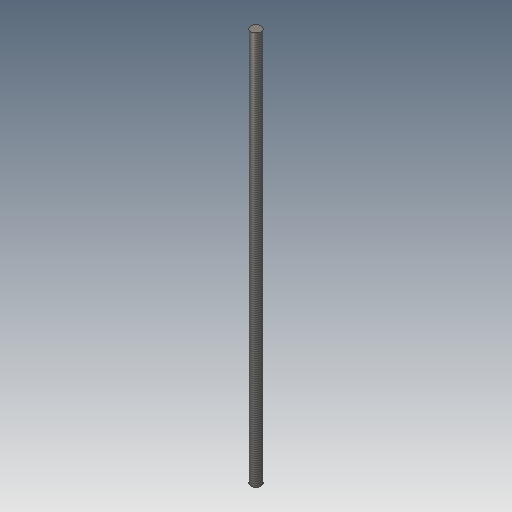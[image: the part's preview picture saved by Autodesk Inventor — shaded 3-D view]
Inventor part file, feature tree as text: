
AUTODESK INVENTOR PART (.ipt)
format: ipt  version: 2019 (Build 230136000, 136)  size: 87,552 bytes
history: native  units: mm
features: extrude x1, thread x1, sketch x1
ambient origin geometry x8: Origin, YZ Plane, XZ Plane, XY Plane, X Axis, Y Axis, Z Axis, Center Point
bodies: Solid1 (feature_tree)
feature tree (3):
  extrude  "Extrusion1"  Depth=300.0mm TaperAngle=0.0deg
  thread  "Thread1"  [1 undecoded]
  sketch  "Sketch1"  dims[d0=8.0mm d1=300.0mm d2=0.0mm d3=10.0mm d4=0.0mm]
note: 1 required parameter value undecoded (feature->parameter linkage not recoverable at this tier; creation-order binding heuristic only, values carry confidence <= 0.55)
